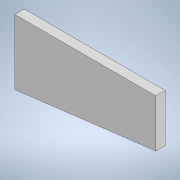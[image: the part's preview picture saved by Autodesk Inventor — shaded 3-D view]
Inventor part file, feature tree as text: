
AUTODESK INVENTOR PART (.ipt)
format: ipt  version: 2020.1 (Build 241239000, 239)  size: 91,648 bytes
history: native  units: in
note: dims shown in document units (in); Inventor stores cm internally (conversion verified against a paired STEP export)
features: extrude x1, sketch x1
ambient origin geometry x8: Origin, YZ Plane, XZ Plane, XY Plane, X Axis, Y Axis, Z Axis, Center Point
bodies: Solid1 (feature_tree)
feature tree (2):
  extrude  "Extrusion1"  Depth=83.0216in
  sketch  "Sketch1"  dims[d0=180.0in d1=72.0in d2=12.0in d3=0.0in d4=181.3447in d5=83.0216in d6=60.9784in]
